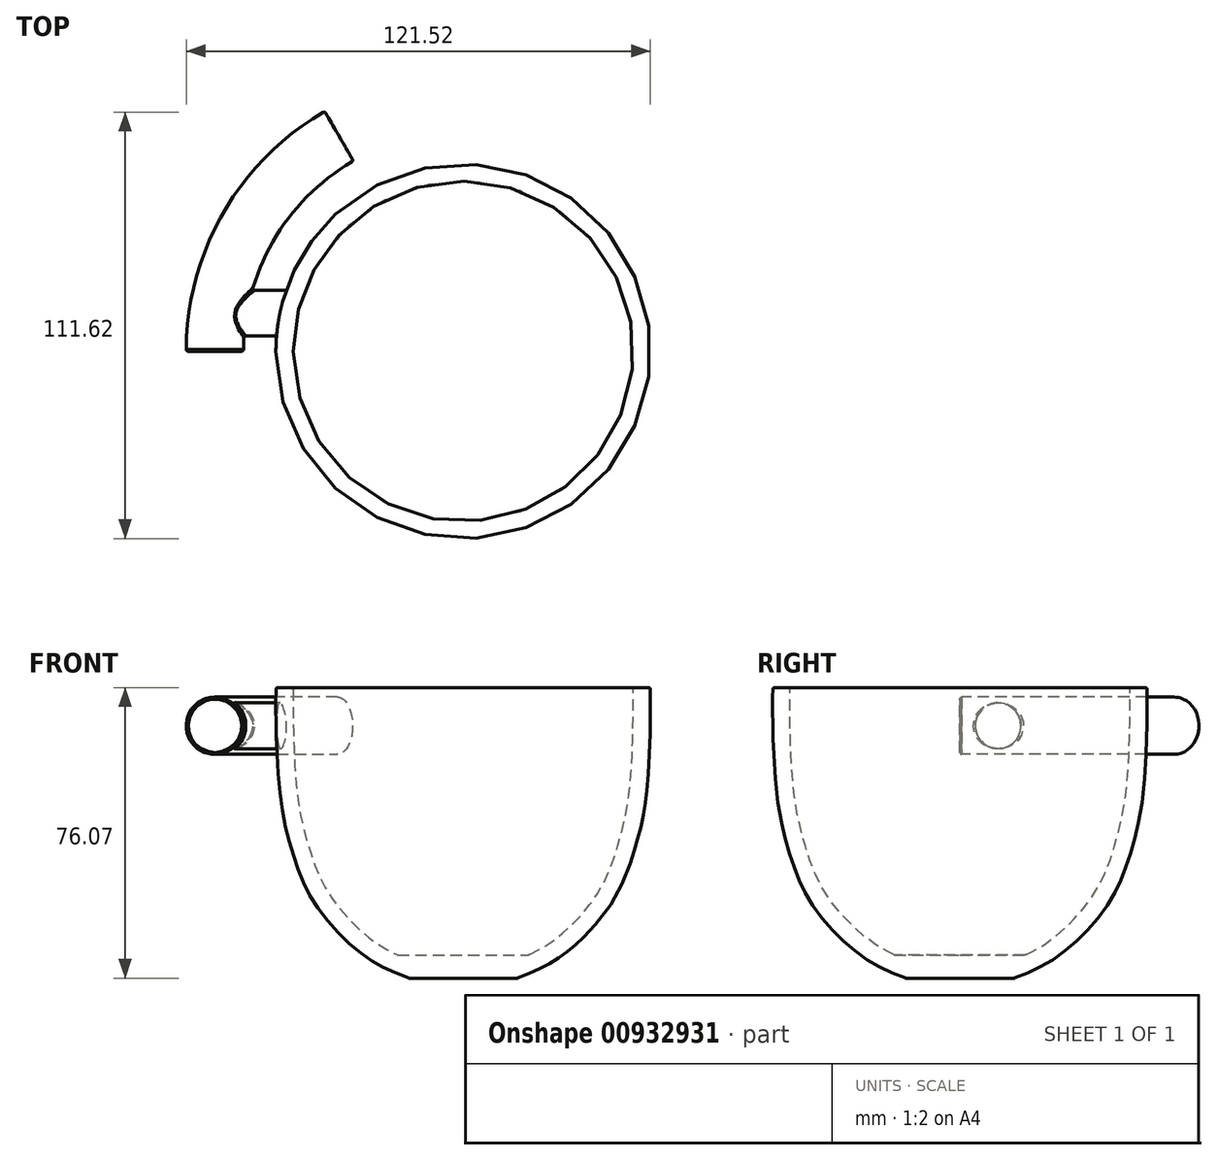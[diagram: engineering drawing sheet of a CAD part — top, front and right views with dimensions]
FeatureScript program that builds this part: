
annotation { "Feature Type Name" : "Feature", "Feature Type Description" : "" }
export const myFeature = defineFeature(function(context is Context, id is Id, definition is map)
    precondition{}
    {
        {
            var Q0;
            Q0=qCreatedBy(makeId("Front.planeOp"),FACE);
            var sketch = newSketch(context, id + "F0", { "sketchPlane" : qUnion([Q0])});
            skLineSegment(sketch, "E0", {"start": v(0, 78.82) * mm, "end": v(-49, 78.82) * mm});
            skLineSegment(sketch, "E1", {"start": v(0, 0) * mm, "end": v(0, 78.82) * mm});
            skFitSpline(sketch, "E2", {"points": [v(-49, 78.82) * mm, v(-49, 71.2) * mm, v(-47.95, 50.94) * mm, v(-44.24, 34.32) * mm, v(-38.54, 21.8) * mm, v(-27.37, 9.77) * mm, v(-17.3, 3.96) * mm, v(0, 0) * mm], "startDerivative": vector(-0.53, -120.05) * mm, "endDerivative": vector(126.32, 0) * mm});
            skSolve(sketch);
        }
        {
            var Q0;
            Q0=qSketchRegion(id+"F0",true);
            var Q1;
            Q1=sQuery(id+"F0.wireOp",EDGE,"E1");
            revolve(context, id + "F1", {"surfaceOperationType" : NewSurfaceOperationType.NEW, "entities" : qUnion([Q0]), "axis" : qUnion([Q1]), "revolveType" : RevolveType.FULL});
        }
        {
            var Q0;
            Q0=makeQuery(id+"F1.opRevolve","SWEPT_FACE",FACE,{"disambiguationData":[OSD([sQuery(id+"F0.wireOp",EDGE,"E0")])]});
            shell(context, id + "F2", {"entities" : qUnion([Q0]), "thickness" : 4.5 * mm});
        }
        {
            var Q0;
            Q0=makeQuery(id+"F1.opRevolve","SWEPT_EDGE",EDGE,{"disambiguationData":[OSD([sQuery(id+"F0.wireOp",EDGE,"E0"),sQuery(id+"F0.wireOp",EDGE,"E2")])]});
            var Q1;
            Q1=makeQuery(id+"F2.opShell","OFFSET_EDGE",EDGE,{"disambiguationData":[OSD([sQuery(id+"F0.wireOp",EDGE,"E0"),sQuery(id+"F0.wireOp",EDGE,"E2")])]});
            fillet(context, id + "F3", {"entities" : qUnion([Q0, Q1]), "radius" : .5 * mm, "tangentPropagation" : true, "defaultsChanged" : true, "vertexSettings" : [], "allowEdgeOverflow" : false});
        }
        {
            var Q0;
            Q0=qCreatedBy(makeId("Front.planeOp"),FACE);
            var sketch = newSketch(context, id + "F4", { "sketchPlane" : qUnion([Q0])});
            skLineSegment(sketch, "E3", {"start": v(-41.77, 30.38) * mm, "end": v(-53.43, 30.38) * mm});
            skLineSegment(sketch, "E4", {"start": v(-49.23, 20.12) * mm, "end": v(-36.53, 20.12) * mm});
            skLineSegment(sketch, "E5", {"start": v(-36.53, 20.12) * mm, "end": v(-41.77, 30.38) * mm});
            skFitSpline(sketch, "E6", {"points": [v(-42.03, 8) * mm, v(-47.44, 16.94) * mm, v(-49.23, 20.12) * mm, v(-51.33, 24.44) * mm, v(-53.43, 30.38) * mm, v(-55.23, 38.72) * mm, v(-56.67, 49.18) * mm, v(-57.32, 61.86) * mm, v(-57.58, 68.13) * mm, v(-57.6, 68.09) * mm], "startDerivative": vector(-47.1, 69.03) * mm, "endDerivative": vector(-6.03, -13.35) * mm});
            skLineSegment(sketch, "E7", {"start": v(-57.58, 68.13) * mm, "end": v(-69.83, 68.13) * mm});
            skFitSpline(sketch, "E8", {"points": [v(-69.83, 68.13) * mm, v(-69.83, 61.07) * mm, v(-69.06, 51.29) * mm, v(-67.63, 40.46) * mm, v(-65.54, 31.18) * mm, v(-63.64, 25) * mm, v(-58.64, 14.66) * mm, v(-54.3, 8) * mm], "startDerivative": vector(-1.12, -53.42) * mm, "endDerivative": vector(31.44, -44.67) * mm});
            skLineSegment(sketch, "E9", {"start": v(-54.3, 8) * mm, "end": v(-42.03, 8) * mm});
            skSolve(sketch);
        }
        {
            var Q0;
            Q0=qCreatedBy(makeId("Right.planeOp"),FACE);
            cPlane(context, id + "F5", {"entities" : qUnion([Q0]), "cplaneType" : CPlaneType.OFFSET, "offset" : 65 * mm, "oppositeDirection" : true, "width" : 150 * mm, "height" : 150 * mm});
        }
        {
            var Q0;
            Q0=qCreatedBy(id+"F5.planeOp",FACE);
            var sketch = newSketch(context, id + "F6", { "sketchPlane" : qUnion([Q0])});
            skPoint(sketch, "E10.middle", {"position": v(0, 24.44) * mm});
            skCircle(sketch, "E11", {"center": v(10, 68.82) * mm, "radius": 6 * mm});
            skSolve(sketch);
        }
        {
            var Q0;
            Q0=qCreatedBy(makeId("Top.planeOp"),FACE);
            cPlane(context, id + "F7", {"entities" : qUnion([Q0]), "cplaneType" : CPlaneType.OFFSET, "offset" : 8 * mm, "width" : 150 * mm, "height" : 150 * mm});
        }
        {
            var Q0;
            Q0=qCreatedBy(id+"F7.planeOp",FACE);
            var sketch = newSketch(context, id + "F8", { "sketchPlane" : qUnion([Q0])});
            skPoint(sketch, "E12.middle", {"position": v(-48.17, 0) * mm});
            skCircle(sketch, "E13", {"center": v(-48.17, 0) * mm, "radius": 7.5 * mm});
            skSolve(sketch);
        }
        {
            var Q0;
            Q0=qCreatedBy(makeId("Front.planeOp"),FACE);
            var sketch = newSketch(context, id + "F9", { "sketchPlane" : qUnion([Q0])});
            skLineSegment(sketch, "E14", {"start": v(0, 1.35) * mm, "end": v(0, 8.85) * mm});
            skLineSegment(sketch, "E15", {"start": v(0, 8.85) * mm, "end": v(-21, 8.85) * mm});
            skLineSegment(sketch, "E16", {"start": v(-21, 8.85) * mm, "end": v(0, 1.35) * mm});
            skSolve(sketch);
        }
        {
            var Q0;
            Q0=qSketchRegion(id+"F9",true);
            var Q1;
            Q1=sQuery(id+"F9.wireOp",EDGE,"E14");
            revolve(context, id + "F10", {"operationType" : NewBodyOperationType.ADD, "surfaceOperationType" : NewSurfaceOperationType.NEW, "entities" : qUnion([Q0]), "axis" : qUnion([Q1]), "revolveType" : RevolveType.FULL});
        }
        {
            var Q0;
            Q0=qCreatedBy(makeId("Front.planeOp"),FACE);
            var sketch = newSketch(context, id + "F11", { "sketchPlane" : qUnion([Q0])});
            skLineSegment(sketch, "E17.bottom", {"start": v(20, 0) * mm, "end": v(-20, 0) * mm});
            skLineSegment(sketch, "E17.top", {"start": v(20, 2.75) * mm, "end": v(-20, 2.75) * mm});
            skLineSegment(sketch, "E17.left", {"start": v(20, 0) * mm, "end": v(20, 2.75) * mm});
            skLineSegment(sketch, "E17.right", {"start": v(-20, 0) * mm, "end": v(-20, 2.75) * mm});
            skSolve(sketch);
        }
        {
            var Q0;
            Q0=qSketchRegion(id+"F11",true);
            extrude(context, id + "F12", {"entities" : qUnion([Q0]), "operationType" : NewBodyOperationType.REMOVE, "oppositeDirection" : true, "depth" : 40 * mm, "offsetDistance" : 25 * mm, "symmetric" : true});
        }
        {
            var Q0;
            Q0=qCreatedBy(makeId("Front.planeOp"),FACE);
            var sketch = newSketch(context, id + "F13", { "sketchPlane" : qUnion([Q0])});
            skCircle(sketch, "E18", {"center": v(-65, 68.82) * mm, "radius": 7.5 * mm});
            skSolve(sketch);
        }
        {
            var Q0;
            Q0=makeQuery(id+"F6.imprint","IMPRINT",FACE,{"disambiguationData":[TD([[makeQuery(id+"F6.imprint","IMPRINT",EDGE,{"derivedFrom":sQuery(id+"F6.wireOp",EDGE,"E11")}),1.0]])]});
            extrude(context, id + "F14", {"entities" : qUnion([Q0]), "operationType" : NewBodyOperationType.ADD, "endBound" : BoundingType.UP_TO_NEXT, "depth" : 25 * mm, "offsetDistance" : 25 * mm});
        }
        {
            var Q0;
            Q0=qCreatedBy(makeId("Top.planeOp"),FACE);
            var sketch = newSketch(context, id + "F15", { "sketchPlane" : qUnion([Q0])});
            skArc(sketch, "E19", {"start": v(-32.5, 56.3) * mm, "mid": v(-56.3, 32.5) * mm, "end": v(-65, 0) * mm});
            skLineSegment(sketch, "E20", {"start": v(0, 0) * mm, "end": v(-65, 0) * mm, "construction": true});
            skLineSegment(sketch, "E21", {"start": v(0, 0) * mm, "end": v(-32.5, 56.3) * mm, "construction": true});
            skSolve(sketch);
        }
        {
            var Q0;
            Q0=makeQuery(id+"F13.imprint","IMPRINT",FACE,{"disambiguationData":[TD([[makeQuery(id+"F13.imprint","IMPRINT",EDGE,{"derivedFrom":sQuery(id+"F13.wireOp",EDGE,"E18")}),1.0]])]});
            var Q1;
            Q1=sQuery(id+"F15.wireOp",EDGE,"E19");
            sweep(context, id + "F16", {"operationType" : NewBodyOperationType.ADD, "profiles" : qUnion([Q0]), "path" : qUnion([Q1])});
        }
        {
            var Q0;
            Q0=makeQuery(id+"F12.boolean.opBoolean","INTERSECT",EDGE,{"derivedFrom":[makeQuery(id+"F1.opRevolve","SWEPT_FACE",FACE,{"disambiguationData":[OSD([sQuery(id+"F0.wireOp",EDGE,"E2")])]}),makeQuery(id+"F12.opExtrude","SWEPT_FACE",FACE,{"disambiguationData":[OSD([sQuery(id+"F11.wireOp",EDGE,"E17.top")])]})]});
            var Q1;
            Q1=makeQuery(id+"F10.boolean.opBoolean","INTERSECT",EDGE,{"derivedFrom":[makeQuery(id+"F2.opShell","OFFSET_FACE",FACE,{"disambiguationData":[OSD([sQuery(id+"F0.wireOp",EDGE,"E2")])]}),makeQuery(id+"F10.opRevolve","SWEPT_FACE",FACE,{"disambiguationData":[OSD([sQuery(id+"F9.wireOp",EDGE,"E15")])]})]});
            var Q2;
            Q2=makeQuery(id+"F14.opExtrude","CAP_EDGE",EDGE,{"disambiguationData":[OSD([sQuery(id+"F6.wireOp",EDGE,"E11")])],"isStart":false});
            var Q3;
            Q3=makeQuery(id+"F16.boolean.opBoolean","INTERSECT",EDGE,{"derivedFrom":[makeQuery(id+"F14.opExtrude","SWEPT_FACE",FACE,{"disambiguationData":[OSD([sQuery(id+"F6.wireOp",EDGE,"E11")])]}),makeQuery(id+"F16.opSweep","SWEPT_FACE",FACE,{"disambiguationData":[OSD([sQuery(id+"F13.wireOp",EDGE,"E18"),sQuery(id+"F15.wireOp",EDGE,"E19")])]})]});
            var Q4;
            Q4=makeQuery(id+"F16.opSweep","CAP_EDGE",EDGE,{"disambiguationData":[OSD([sQuery(id+"F13.wireOp",EDGE,"E18"),sQuery(id+"F15.wireOp",VERTEX,"E19.end")])],"isStart":true});
            var Q5;
            Q5=makeQuery(id+"F16.opSweep","CAP_FACE",FACE,{"disambiguationData":[OSD([sQuery(id+"F13.wireOp",EDGE,"E18"),sQuery(id+"F15.wireOp",VERTEX,"E19.start")])],"isStart":false});
            fillet(context, id + "F17", {"entities" : qUnion([Q0, Q1, Q2, Q3, Q4, Q5]), "tangentPropagation" : true, "radius" : .5 * mm, "defaultsChanged" : false, "vertexSettings" : [], "allowEdgeOverflow" : false});
        }
    });
